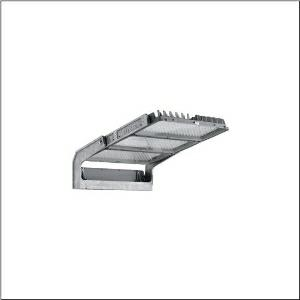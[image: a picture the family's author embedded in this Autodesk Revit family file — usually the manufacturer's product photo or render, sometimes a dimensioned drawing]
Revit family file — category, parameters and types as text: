
# Revit family: floodlight_fl_11_maxi_pro___rs08_5xa779229l01gb_31ec
name_source: partatom
category: Lighting Fixtures
units: mm (PartAtom-declared; Revit-internal decimal feet)

## family parameters
Cut with Voids When Loaded = No
Host = Face
Light Source = No
Part Type = Normal
Room Calculation Point = No
Round Connector Dimension = Use Diameter
Shared = No

## types (1)
- --- (1 x LED, 163120 lm, 1315 W, 5700K)
    Apparent Load = 1315 VA
    CIE Flux Codes = 70 87 98 100 100
    Color Rendering = 70
    Color Temperature = 5700K
    Default Elevation = 1800 mm
    Description = Floodlight FL 11  maxi  pro floodlight; light control with lens of PMMA; cover panel of toughened safety glass, transparent; light distribution: RS08, rotationally symmetric direct distribution, LEDcolour temperature: 5700K, rated luminous flux: 163.120lm, colour rendering: CRI > 70, light colour: 757; luminous efficacy: 124lm/W; brightness control: DMX+RDM; with terminal, 6-pole, max. 2.5mm², mains connection: 220..240V/380..400V AC, 50/60Hz, surge voltage resistance: line to ground: 10kV, service life up to 100,000h L90. Typical operating time: 1000h per year, ECG replaceable separately, LED unit replaceable without ESD environment, dustproof LED module, dimming range 10..100%; 1315W floodlight with 3x LED unit of diecast aluminium, coated grey; length: 1.003mm / width: 651mm / height: 338mm; mounting bracket, of diecast aluminium, uncoated, natural, protection rating (complete): IP66; insulation class (complete): insulation class I (protective earthing); certification: CE, ENEC, VDE; ball protection: ball impact resistant, only for outdoor installations in the designated locations, permissible operating ambient temperature: -45..+55°C, permissible storage temperature: -40..+85°Cpackaging unit: 1 piece

Light Distribution: RS08
    Height = 320 mm
    Lamp = 1 x LED
    Lamp Light Flux = 163120 lm
    Lamp Power = 1315 W
    Lamp count = 1
    Length = 1002 mm
    Luminous efficacy = 124 lm/W
    Manufacturer = Siteco
    ModVariant = No
    Model = 5XA779229L01GB
    Mounting Place = Ceiling
    Mounting Type = Surface mounted
    Number of Poles = 1
    OnlyDefault = Yes
    Power Factor = 1
    Product Name = Floodlight FL 11 maxi pro | RS08
    Product group = floodlight | ceiling mounted
    ProductGroupID = 301
    Protection Class = Protection class I
    Protection Degree = IP 66
    RLX_Detail_Level = 1
    RLX_Emergency_Light_Flux = 0 lm
    RLX_Emergency_Type = 0
    RLX_Emergency_Type_DB = No
    RlxData = <blob elided: 40545 chars, md5=abeebe10>
    Socket = socket
    Standby Power = 0 W
    System Light Flux = 163120 lm
    System Power = 1315 W
    Type Comments = factory setting: luminous flux: 100 % | dim-lin: 255 | 895 mA
    Type Image = l_1356210.jpg
    URL = http://relux.com
    VarID = @adj_014217
    Voltage = 0 V
    Weight = 0.00 kg
    Width = 655 mm

## geometry (parser evidence)
native form markers: Blend x4, Sweep x10
no freeform markers — native parametric forms only
